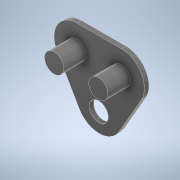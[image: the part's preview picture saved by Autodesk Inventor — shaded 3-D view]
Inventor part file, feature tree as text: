
AUTODESK INVENTOR PART (.ipt)
format: ipt  version: 2022 (Build 260153000, 153)  size: 141,312 bytes
history: native  units: in
note: dims shown in document units (in); Inventor stores cm internally (conversion verified against a paired STEP export)
features: extrude x2, sketch x2, other x1
ambient origin geometry x8: Origin, YZ Plane, XZ Plane, XY Plane, X Axis, Y Axis, Z Axis, Center Point
bodies: Body1 (feature_tree)
feature tree (5):
  other  "Sólido1"
  extrude  "Extrusión1"  Depth=0.0984in
  extrude  "Extrusión2"  Depth=0.1181in
  sketch  "Boceto1"  dims[d2=0.0984in d9=0.0984in]
  sketch  "Boceto3"  dims[d10=0.2496in d13=0.0984in d14=0.2157in d15=0.1228in d16=60.0deg d17=60.0deg d18=60.0deg d19=0.1181in d20=0.0236in d21=0.0in d22=0.0984in d23=0.0984in d24=0.1181in d25=0.0in]
